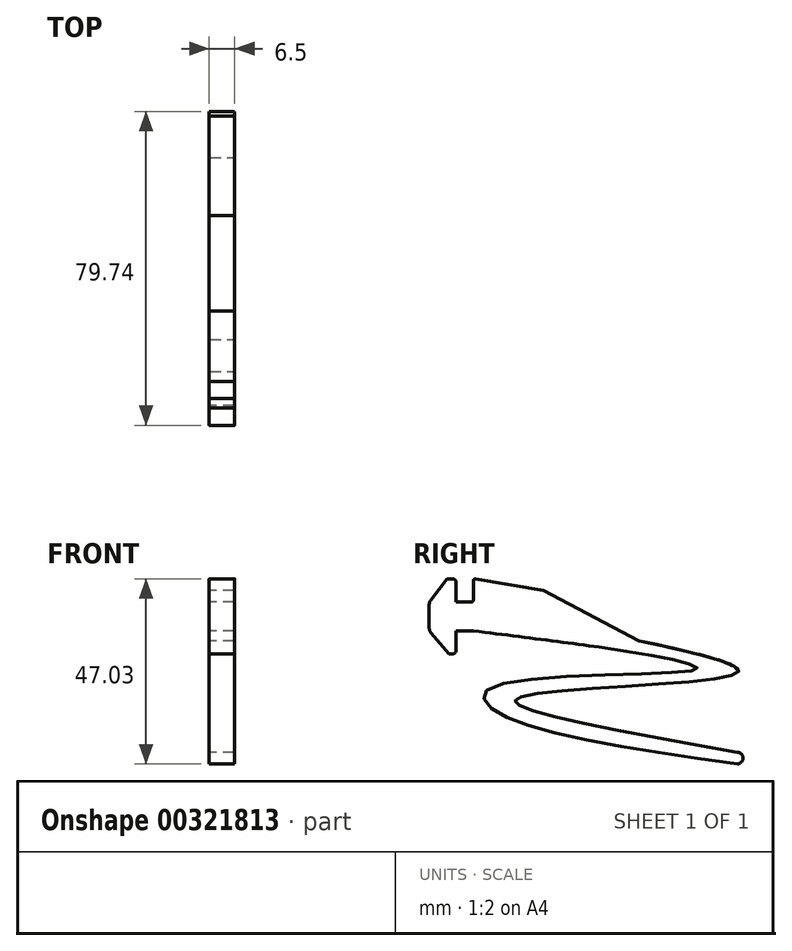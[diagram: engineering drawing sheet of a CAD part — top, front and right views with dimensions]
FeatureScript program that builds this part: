
annotation { "Feature Type Name" : "Feature", "Feature Type Description" : "" }
export const myFeature = defineFeature(function(context is Context, id is Id, definition is map)
    precondition{}
    {
        {
            var Q0;
            Q0=qCreatedBy(makeId("Right.planeOp"),FACE);
            var sketch = newSketch(context, id + "F0", { "sketchPlane" : qUnion([Q0])});
            skLineSegment(sketch, "E0", {"start": v(-2.33, 1.82) * mm, "end": v(-6.7, 1.82) * mm});
            skLineSegment(sketch, "E1", {"start": v(-6.7, 1.82) * mm, "end": v(-6.7, 6.9) * mm});
            skLineSegment(sketch, "E2", {"start": v(-7.5, 7.7) * mm, "end": v(-9.05, 7.7) * mm});
            skLineSegment(sketch, "E3", {"start": v(-9.05, 7.7) * mm, "end": v(-13.12, 2.38) * mm});
            skLineSegment(sketch, "E4", {"start": v(-13.53, 1.17) * mm, "end": v(-13.53, -4.71) * mm});
            skLineSegment(sketch, "E5", {"start": v(-13.05, -6.02) * mm, "end": v(-8.5, -11.3) * mm});
            skLineSegment(sketch, "E6", {"start": v(-8.5, -11.3) * mm, "end": v(-7.5, -11.3) * mm});
            skLineSegment(sketch, "E7", {"start": v(-6.7, -10.5) * mm, "end": v(-6.7, -5.43) * mm});
            skLineSegment(sketch, "E8", {"start": v(-6.7, -5.43) * mm, "end": v(-2.33, -5.43) * mm});
            skLineSegment(sketch, "E9", {"start": v(-2.33, 7.82) * mm, "end": v(-2.33, 1.82) * mm});
            skLineSegment(sketch, "E10", {"start": v(-6.7, 1.82) * mm, "end": v(-6.7, -5.43) * mm, "construction": true});
            skLineSegment(sketch, "E11", {"start": v(-6.7, -1.8) * mm, "end": v(-13.53, -1.8) * mm, "construction": true});
            skPoint(sketch, "E12.visualSharp", {"position": v(-6.7, -11.3) * mm});
            skArc(sketch, "E12.filletArc", {"start": v(-7.5, -11.3) * mm, "mid": v(-6.94, -11.07) * mm, "end": v(-6.7, -10.5) * mm});
            skPoint(sketch, "E13.visualSharp", {"position": v(-6.7, 7.7) * mm});
            skArc(sketch, "E13.filletArc", {"start": v(-6.7, 6.9) * mm, "mid": v(-6.94, 7.46) * mm, "end": v(-7.5, 7.7) * mm});
            skPoint(sketch, "E14.visualSharp", {"position": v(-13.53, 1.85) * mm});
            skArc(sketch, "E14.filletArc", {"start": v(-13.12, 2.38) * mm, "mid": v(-13.42, 1.8) * mm, "end": v(-13.53, 1.17) * mm});
            skPoint(sketch, "E15.visualSharp", {"position": v(-13.53, -5.45) * mm});
            skArc(sketch, "E15.filletArc", {"start": v(-13.53, -4.71) * mm, "mid": v(-13.4, -5.4) * mm, "end": v(-13.05, -6.02) * mm});
            skLineSegment(sketch, "E16", {"start": v(9.13, -1.8) * mm, "end": v(-6.7, -1.8) * mm, "construction": true});
            skFitSpline(sketch, "E17", {"points": [v(9.13, -1.8) * mm, v(64.2, -16.5) * mm, v(9.13, -22.48) * mm, v(64.81, -36.3) * mm], "startDerivative": vector(275.11, -55.48) * mm, "endDerivative": vector(277.32, -50.3) * mm});
            skFitSpline(sketch, "E18", {"points": [v(64.81, -39.3) * mm, v(2.43, -25.24) * mm, v(1.7, -20.13) * mm, v(54.26, -15.3) * mm, v(49.66, -13.08) * mm, v(-2.33, -5.43) * mm], "startDerivative": vector(-274.98, 37.46) * mm, "endDerivative": vector(-230.34, 30.46) * mm});
            skLineSegment(sketch, "E19", {"start": v(-2.33, 7.82) * mm, "end": v(15.56, 4.82) * mm});
            skPoint(sketch, "E19.endSnap0", {"position": v(-2.33, 4.82) * mm});
            skLineSegment(sketch, "E20", {"start": v(15.56, 4.82) * mm, "end": v(39.8, -8) * mm});
            skArc(sketch, "E21", {"start": v(64.81, -39.3) * mm, "mid": v(66.2, -37.8) * mm, "end": v(64.81, -36.3) * mm});
            skLineSegment(sketch, "E22", {"start": v(-2.33, -5.43) * mm, "end": v(-2.33, -11.43) * mm});
            skLineSegment(sketch, "E23", {"start": v(-2.33, -11.43) * mm, "end": v(29.6, -9.6) * mm});
            skSolve(sketch);
        }
        {
            var Q0;
            Q0=makeQuery(id+"F0.imprint","IMPRINT",FACE,{"disambiguationData":[TD([[makeQuery(id+"F0.imprint","IMPRINT",EDGE,{"derivedFrom":sQuery(id+"F0.wireOp",EDGE,"E0")}),1.0]])]});
            extrude(context, id + "F1", {"entities" : qUnion([Q0]), "depth" : 6.5 * mm});
        }
        {
            var Q0;
            Q0=makeQuery(id+"F1.opExtrude","SWEPT_EDGE",EDGE,{"disambiguationData":[OSD([sQuery(id+"F0.wireOp",EDGE,"f4eaedeb-38f5-4612-8851-28724b1d6449"),sQuery(id+"F0.wireOp",EDGE,"E9")])]});
            var Q1;
            Q1=makeQuery(id+"F1.opExtrude","SWEPT_EDGE",EDGE,{"disambiguationData":[OSD([sQuery(id+"F0.wireOp",EDGE,"8ce88e0f-0908-47d8-b751-c5ebdf0c412d"),sQuery(id+"F0.wireOp",EDGE,"cc48a477-5546-4aa7-a1f7-5fc7fe4c0098")])]});
            fillet(context, id + "F2", {"entities" : qUnion([Q0, Q1]), "radius" : .5 * mm, "tangentPropagation" : true, "allowEdgeOverflow" : false});
        }
    });
